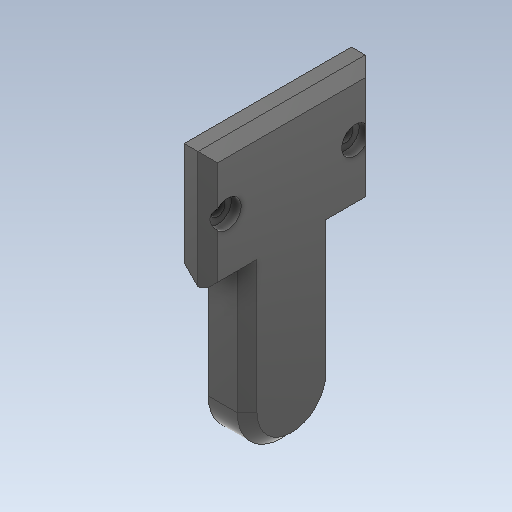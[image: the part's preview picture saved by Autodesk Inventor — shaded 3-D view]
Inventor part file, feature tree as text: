
AUTODESK INVENTOR PART (.ipt)
format: ipt  version: 2020 (Build 240168000, 168)  size: 205,312 bytes
history: native  units: in
note: dims shown in document units (in); Inventor stores cm internally (conversion verified against a paired STEP export)
features: sketch x19, other x4, plane x2
ambient origin geometry x8: Origin, YZ Plane, XZ Plane, XY Plane, X Axis, Y Axis, Z Axis, Center Point
bodies: Solid1 (feature_tree), Solid2 (feature_tree)
feature tree (25):
  other  "FemurSupportBot.ipt"
  other  "Solid1::FemurSupportBot.ipt"
  other  "Solid2::FemurSupportBot.ipt"
  other  "TaggingFeature1"
  sketch  "Sketch1"  dims[d0=0.3937in]
  sketch  "Sketch2"
  sketch  "Sketch3"
  sketch  "Sketch4"
  sketch  "Sketch5"
  sketch  "Sketch6"
  sketch  "Sketch8"
  sketch  "Sketch10"
  sketch  "Sketch11"
  sketch  "Sketch12"
  sketch  "Sketch13"
  sketch  "Sketch14"
  sketch  "Sketch15"
  sketch  "Sketch17"
  sketch  "Sketch19"
  sketch  "Sketch20"
  sketch  "Sketch21"
  sketch  "Sketch22"
  sketch  "Sketch23"
  plane  "Work Plane1"
  plane  "Work Plane2"
